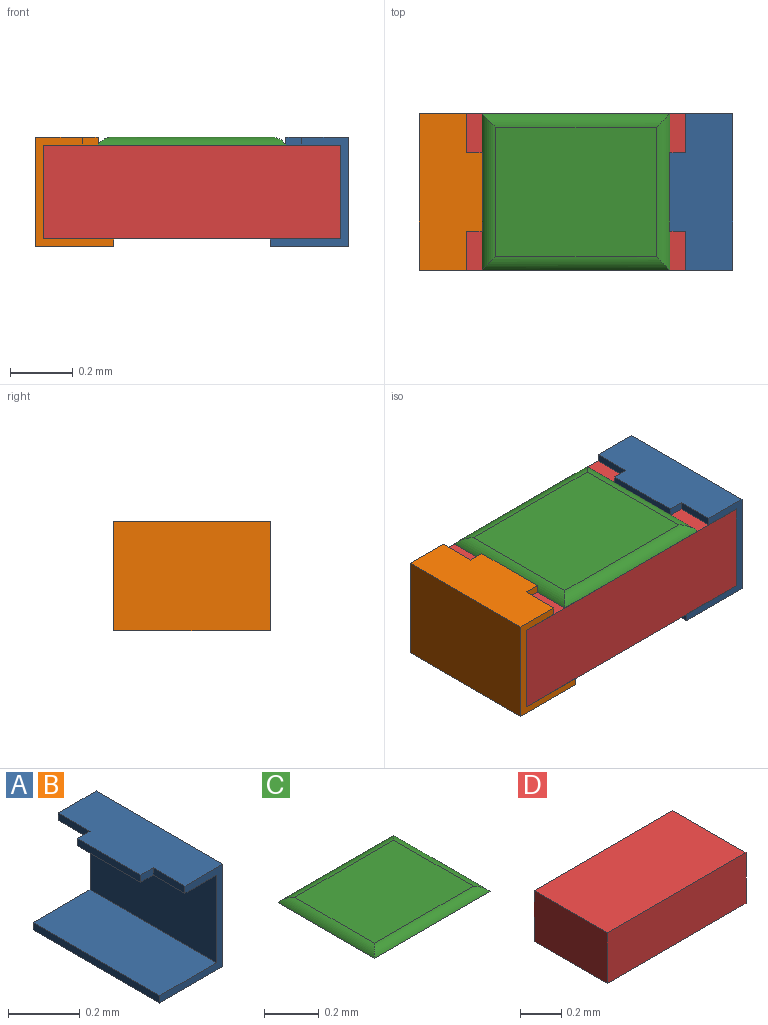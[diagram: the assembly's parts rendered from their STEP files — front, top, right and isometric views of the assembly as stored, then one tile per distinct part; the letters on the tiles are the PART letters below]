
ASSEMBLY  parts=4 mates=3
PART A: 14 faces, bbox 0.3x0.5x0.4 mm
  f0: plane 0.5x0.03mm, normal (-1,0,0), area 0mm2, adj f1,f3,f5,f7
  f1: plane 0.35x0.25mm, normal (0,-1,0), area 0mm2, adj f0,f2,f4,f5,f6,f7,f8,f10
  f2: plane 0.5x0.35mm, normal (1,0,0), area 0.2mm2, adj f1,f3,f4,f5
  f3: plane 0.35x0.25mm, normal (0,1,0), area 0mm2, adj f0,f2,f4,f5,f6,f7,f8,f9
  f4: plane 0.5x0.2mm, normal (0,0,1), area 0.1mm2, adj f1,f2,f3,f9,f10,f11,f12,f13
  f5: plane 0.5x0.25mm, normal (0,0,-1), area 0.1mm2, adj f0,f1,f2,f3
  f6: plane 0.5x0.18mm, normal (0,0,-1), area 0.1mm2, adj f1,f3,f8,f9,f10,f11,f12,f13
  f7: plane 0.5x0.23mm, normal (0,0,1), area 0.1mm2, adj f0,f1,f3,f8
  f8: plane 0.5x0.3mm, normal (-1,0,0), area 0.1mm2, adj f1,f3,f6,f7
  f9: plane 0.13x0.03mm, normal (-1,0,0), area 0mm2, adj f3,f4,f6,f13
  f10: plane 0.13x0.03mm, normal (-1,0,0), area 0mm2, adj f1,f4,f6,f11
  f11: plane 0.05x0.03mm, normal (0,-1,0), area 0mm2, adj f4,f6,f10,f12
  f12: plane 0.25x0.03mm, normal (-1,0,0), area 0mm2, adj f4,f6,f11,f13
  f13: plane 0.05x0.03mm, normal (0,1,0), area 0mm2, adj f4,f6,f9,f12
PART B: same geometry as A
PART C: 6 faces, bbox 0.6x0.5x0 mm
  f0: plane 0.51x0.41mm, normal (0,0,1), area 0.2mm2, adj f2,f3,f4,f5
  f1: plane 0.6x0.5mm, normal (0,0,-1), area 0.3mm2, adj f2,f3,f4,f5
  f2: cylinder r=0.05mm len=0.6mm, axis (-1,0,0), area 0mm2, adj f0,f1,f3,f4
  f3: cylinder r=0.05mm len=0.5mm, axis (0,1,0), area 0mm2, adj f0,f1,f2,f5
  f4: cylinder r=0.05mm len=0.5mm, axis (0,1,0), area 0mm2, adj f0,f1,f2,f5
  f5: cylinder r=0.05mm len=0.6mm, axis (-1,0,0), area 0mm2, adj f0,f1,f3,f4
PART D: 6 faces, bbox 1x0.5x0.3 mm
  f0: plane 0.5x0.3mm, normal (1,0,0), area 0.1mm2, adj f1,f3,f4,f5
  f1: plane 0.95x0.3mm, normal (0,1,0), area 0.3mm2, adj f0,f2,f4,f5
  f2: plane 0.5x0.3mm, normal (-1,0,0), area 0.1mm2, adj f1,f3,f4,f5
  f3: plane 0.95x0.3mm, normal (0,-1,0), area 0.3mm2, adj f0,f2,f4,f5
  f4: plane 0.95x0.5mm, normal (0,0,1), area 0.5mm2, adj f0,f1,f2,f3
  f5: plane 0.95x0.5mm, normal (0,0,-1), area 0.5mm2, adj f0,f1,f2,f3
PLACE A t=(0.38,0,-0.03)mm
PLACE B rot(axis=(0,0,1),180deg) t=(-0.38,0,-0.03)mm
PLACE C rot(axis=(0,0,1),180deg) t=(0,0,0.3)mm
PLACE D at identity
MATE fastened A.f8 <-> D.f0  axis (-1,0,0) through (0.48,0,0.15)mm
MATE fastened B.f8 <-> D.f2  axis (1,0,0) through (-0.47,0,0.15)mm
MATE fastened C.f1 <-> D.f4  axis (0,0,-1) through (0,0,0.3)mm
